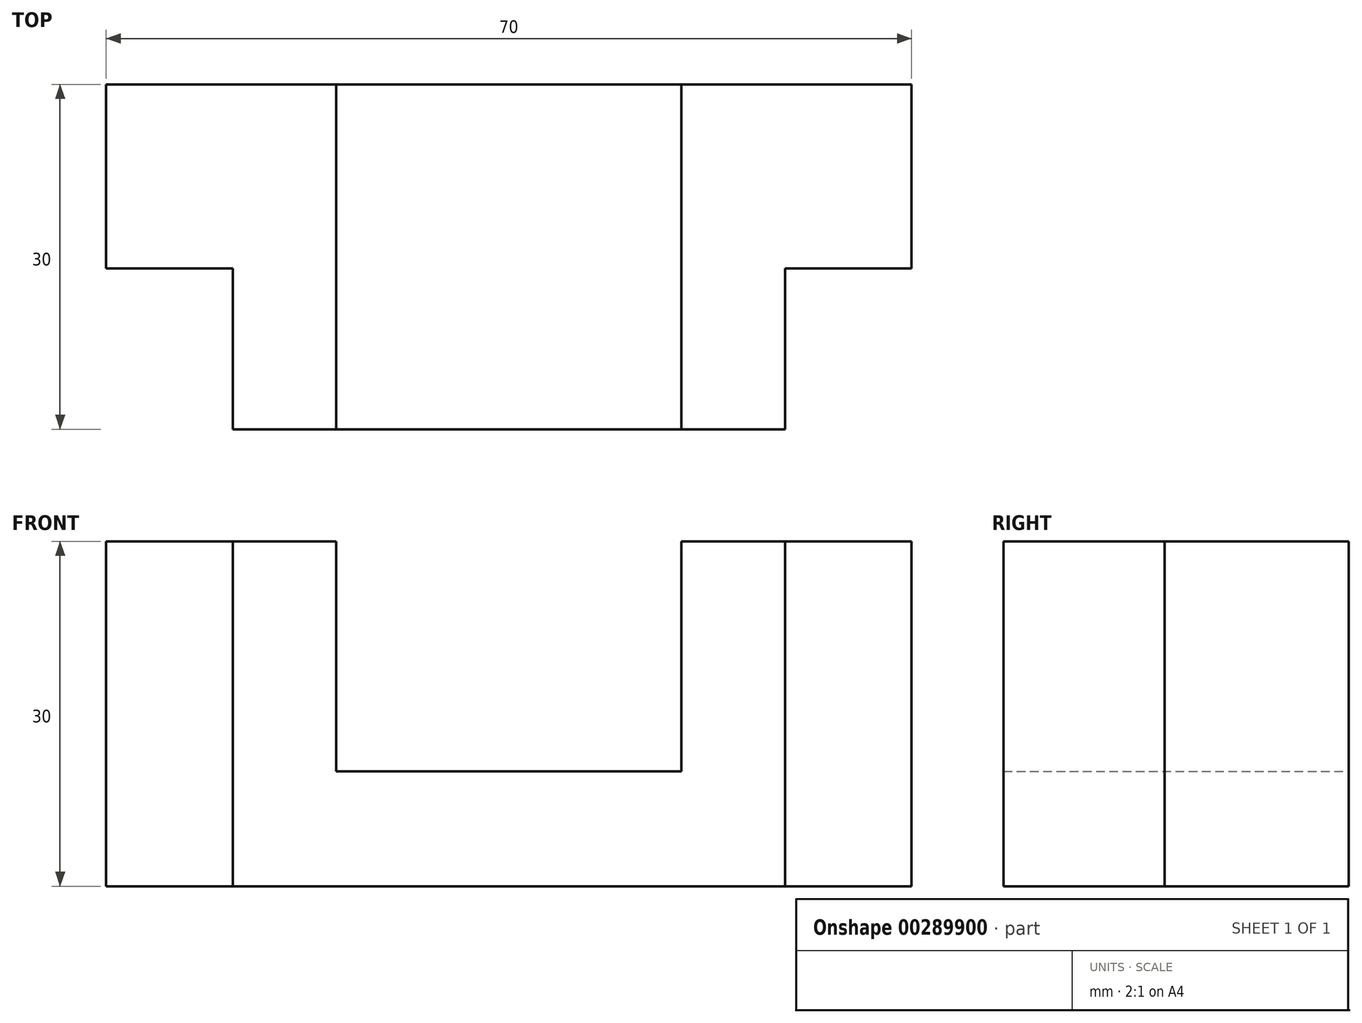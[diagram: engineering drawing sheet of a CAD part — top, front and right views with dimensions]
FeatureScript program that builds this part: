
annotation { "Feature Type Name" : "Feature", "Feature Type Description" : "" }
export const myFeature = defineFeature(function(context is Context, id is Id, definition is map)
    precondition{}
    {
        {
            var Q0;
            Q0=qCreatedBy(makeId("Top.planeOp"),FACE);
            var sketch = newSketch(context, id + "F0", { "sketchPlane" : qUnion([Q0])});
            skLineSegment(sketch, "E0", {"start": v(-53.82, -40.98) * mm, "end": v(-5.82, -40.98) * mm});
            skLineSegment(sketch, "E1", {"start": v(-5.82, -40.98) * mm, "end": v(-5.82, -26.98) * mm});
            skLineSegment(sketch, "E2", {"start": v(-5.82, -26.98) * mm, "end": v(5.18, -26.98) * mm});
            skLineSegment(sketch, "E3", {"start": v(5.18, -26.98) * mm, "end": v(5.18, -10.98) * mm});
            skLineSegment(sketch, "E4", {"start": v(5.18, -10.98) * mm, "end": v(-64.82, -10.98) * mm});
            skLineSegment(sketch, "E5", {"start": v(-64.82, -10.98) * mm, "end": v(-64.82, -26.98) * mm});
            skLineSegment(sketch, "E6", {"start": v(-64.82, -26.98) * mm, "end": v(-53.82, -26.98) * mm});
            skLineSegment(sketch, "E7", {"start": v(-53.82, -26.98) * mm, "end": v(-53.82, -40.98) * mm});
            skLineSegment(sketch, "E8", {"start": v(-53.82, -40.98) * mm, "end": v(-44.82, -40.98) * mm});
            skLineSegment(sketch, "E9", {"start": v(-44.82, -40.98) * mm, "end": v(-44.82, -10.98) * mm});
            skLineSegment(sketch, "E10", {"start": v(-5.82, -40.98) * mm, "end": v(-14.82, -40.98) * mm});
            skLineSegment(sketch, "E11", {"start": v(-14.82, -40.98) * mm, "end": v(-14.82, -10.98) * mm});
            skSolve(sketch);
        }
        {
            var Q0;
            Q0=makeQuery(id+"F0.imprint","IMPRINT",FACE,{"disambiguationData":[TD([[makeQuery(id+"F0.imprint","IMPRINT",EDGE,{"derivedFrom":sQuery(id+"F0.wireOp",EDGE,"E0")}),1.0]])]});
            extrude(context, id + "F1", {"entities" : qUnion([Q0]), "depth" : 10 * mm});
        }
        {
            var Q0;
            {var subQ0=sQuery(id+"F0.wireOp",EDGE,"E5");Q0=makeQuery(id+"F0.imprint","IMPRINT",FACE,{"disambiguationData":[TD([[makeQuery(id+"F0.imprint","IMPRINT",EDGE,{"derivedFrom":subQ0}),1.0]])]});}
            var Q1;
            Q1=makeQuery(id+"F0.imprint","IMPRINT",FACE,{"disambiguationData":[TD([[makeQuery(id+"F0.imprint","IMPRINT",EDGE,{"derivedFrom":sQuery(id+"F0.wireOp",EDGE,"E1")}),1.0]])]});
            extrude(context, id + "F2", {"entities" : qUnion([Q0, Q1]), "operationType" : NewBodyOperationType.ADD, "depth" : 30 * mm});
        }
    });
